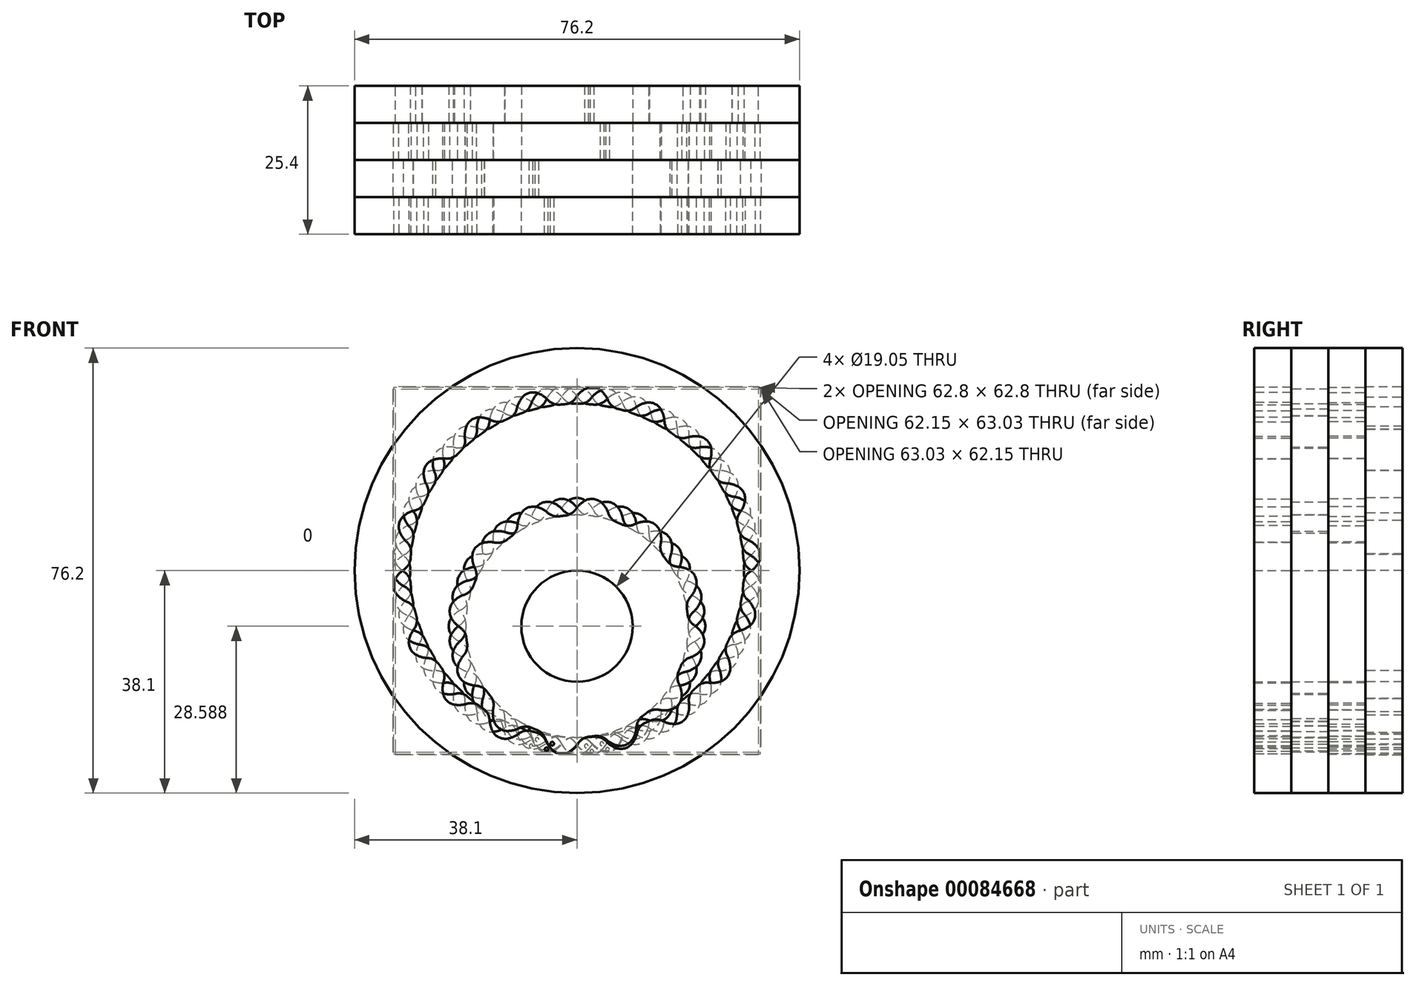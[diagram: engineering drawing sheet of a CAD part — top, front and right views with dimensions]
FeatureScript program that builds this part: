
annotation { "Feature Type Name" : "Feature", "Feature Type Description" : "" }
export const myFeature = defineFeature(function(context is Context, id is Id, definition is map)
    precondition{}
    {
        {
            var Q0;
            Q0=qCreatedBy(makeId("Front.planeOp"),FACE);
            var sketch = newSketch(context, id + "F0", { "sketchPlane" : qUnion([Q0])});
            skCircle(sketch, "E0", {"center": v(0, 0) * mm, "radius": 38.1 * mm});
            skCircle(sketch, "E1", {"center": v(0, 0) * mm, "radius": 28.58 * mm});
            skCircle(sketch, "E2", {"center": v(0, 0) * mm, "radius": 19.05 * mm});
            skCircle(sketch, "E3", {"center": v(0, 0) * mm, "radius": 9.53 * mm});
            skArc(sketch, "E4", {"start": v(0, -22.23) * mm, "mid": v(2.06, -20.95) * mm, "end": v(3.16, -18.79) * mm});
            skArc(sketch, "E5", {"start": v(-3.16, -18.79) * mm, "mid": v(-2.06, -20.95) * mm, "end": v(0, -22.23) * mm});
            skArc(sketch, "E6", {"start": v(0, -31.74) * mm, "mid": v(2.04, -30.5) * mm, "end": v(3.16, -28.4) * mm});
            skArc(sketch, "E7", {"start": v(-3.16, -28.4) * mm, "mid": v(-2.04, -30.5) * mm, "end": v(0, -31.74) * mm});
            skArc(sketch, "E8.1.0", {"start": v(6.65, -17.85) * mm, "mid": v(8.69, -19.17) * mm, "end": v(11.11, -19.25) * mm});
            skArc(sketch, "E8.1.1", {"start": v(11.11, -19.25) * mm, "mid": v(12.26, -17.11) * mm, "end": v(12.13, -14.69) * mm});
            skArc(sketch, "E8.2.0", {"start": v(14.69, -12.13) * mm, "mid": v(17.11, -12.26) * mm, "end": v(19.25, -11.11) * mm});
            skArc(sketch, "E8.2.1", {"start": v(19.25, -11.11) * mm, "mid": v(19.17, -8.69) * mm, "end": v(17.85, -6.65) * mm});
            skArc(sketch, "E8.3.0", {"start": v(18.79, -3.16) * mm, "mid": v(20.95, -2.06) * mm, "end": v(22.23, 0) * mm});
            skArc(sketch, "E8.3.1", {"start": v(22.23, 0) * mm, "mid": v(20.95, 2.06) * mm, "end": v(18.79, 3.16) * mm});
            skArc(sketch, "E8.4.0", {"start": v(17.85, 6.65) * mm, "mid": v(19.17, 8.69) * mm, "end": v(19.25, 11.11) * mm});
            skArc(sketch, "E8.4.1", {"start": v(19.25, 11.11) * mm, "mid": v(17.11, 12.26) * mm, "end": v(14.69, 12.13) * mm});
            skArc(sketch, "E8.5.0", {"start": v(12.13, 14.69) * mm, "mid": v(12.26, 17.11) * mm, "end": v(11.11, 19.25) * mm});
            skArc(sketch, "E8.5.1", {"start": v(11.11, 19.25) * mm, "mid": v(8.69, 19.17) * mm, "end": v(6.65, 17.85) * mm});
            skArc(sketch, "E8.6.0", {"start": v(3.16, 18.79) * mm, "mid": v(2.06, 20.95) * mm, "end": v(0, 22.23) * mm});
            skArc(sketch, "E8.6.1", {"start": v(0, 22.23) * mm, "mid": v(-2.06, 20.95) * mm, "end": v(-3.16, 18.79) * mm});
            skArc(sketch, "E8.7.0", {"start": v(-6.65, 17.85) * mm, "mid": v(-8.69, 19.17) * mm, "end": v(-11.11, 19.25) * mm});
            skArc(sketch, "E8.7.1", {"start": v(-11.11, 19.25) * mm, "mid": v(-12.26, 17.11) * mm, "end": v(-12.13, 14.69) * mm});
            skArc(sketch, "E8.8.0", {"start": v(-14.69, 12.13) * mm, "mid": v(-17.11, 12.26) * mm, "end": v(-19.25, 11.11) * mm});
            skArc(sketch, "E8.8.1", {"start": v(-19.25, 11.11) * mm, "mid": v(-19.17, 8.69) * mm, "end": v(-17.85, 6.65) * mm});
            skArc(sketch, "E8.9.0", {"start": v(-18.79, 3.16) * mm, "mid": v(-20.95, 2.06) * mm, "end": v(-22.23, 0) * mm});
            skArc(sketch, "E8.9.1", {"start": v(-22.23, 0) * mm, "mid": v(-20.95, -2.06) * mm, "end": v(-18.79, -3.16) * mm});
            skArc(sketch, "E8.10.0", {"start": v(-17.85, -6.65) * mm, "mid": v(-19.17, -8.69) * mm, "end": v(-19.25, -11.11) * mm});
            skArc(sketch, "E8.10.1", {"start": v(-19.25, -11.11) * mm, "mid": v(-17.11, -12.26) * mm, "end": v(-14.69, -12.13) * mm});
            skArc(sketch, "E8.11.0", {"start": v(-12.13, -14.69) * mm, "mid": v(-12.26, -17.11) * mm, "end": v(-11.11, -19.25) * mm});
            skArc(sketch, "E8.11.1", {"start": v(-11.11, -19.25) * mm, "mid": v(-8.69, -19.17) * mm, "end": v(-6.65, -17.85) * mm});
            skArc(sketch, "E9.1.0", {"start": v(6.74, -27.77) * mm, "mid": v(8.51, -29.37) * mm, "end": v(10.86, -29.83) * mm});
            skArc(sketch, "E9.1.1", {"start": v(10.86, -29.83) * mm, "mid": v(12.35, -27.97) * mm, "end": v(12.69, -25.6) * mm});
            skArc(sketch, "E9.2.0", {"start": v(15.83, -23.79) * mm, "mid": v(18.05, -24.68) * mm, "end": v(20.4, -24.32) * mm});
            skArc(sketch, "E9.2.1", {"start": v(20.4, -24.32) * mm, "mid": v(21.17, -22.06) * mm, "end": v(20.68, -19.72) * mm});
            skArc(sketch, "E9.3.0", {"start": v(23.01, -16.94) * mm, "mid": v(25.4, -17.02) * mm, "end": v(27.5, -15.87) * mm});
            skArc(sketch, "E9.3.1", {"start": v(27.5, -15.87) * mm, "mid": v(27.44, -13.48) * mm, "end": v(26.18, -11.46) * mm});
            skArc(sketch, "E9.4.0", {"start": v(27.42, -8.05) * mm, "mid": v(29.69, -7.3) * mm, "end": v(31.26, -5.51) * mm});
            skArc(sketch, "E9.4.1", {"start": v(31.26, -5.51) * mm, "mid": v(30.4, -3.29) * mm, "end": v(28.52, -1.82) * mm});
            skArc(sketch, "E9.5.0", {"start": v(28.52, 1.82) * mm, "mid": v(30.4, 3.29) * mm, "end": v(31.26, 5.51) * mm});
            skArc(sketch, "E9.5.1", {"start": v(31.26, 5.51) * mm, "mid": v(29.69, 7.3) * mm, "end": v(27.42, 8.05) * mm});
            skArc(sketch, "E9.6.0", {"start": v(26.18, 11.46) * mm, "mid": v(27.44, 13.48) * mm, "end": v(27.5, 15.87) * mm});
            skArc(sketch, "E9.6.1", {"start": v(27.5, 15.87) * mm, "mid": v(25.4, 17.02) * mm, "end": v(23.01, 16.94) * mm});
            skArc(sketch, "E9.7.0", {"start": v(20.68, 19.72) * mm, "mid": v(21.17, 22.06) * mm, "end": v(20.4, 24.32) * mm});
            skArc(sketch, "E9.7.1", {"start": v(20.4, 24.32) * mm, "mid": v(18.05, 24.68) * mm, "end": v(15.83, 23.79) * mm});
            skArc(sketch, "E9.8.0", {"start": v(12.69, 25.6) * mm, "mid": v(12.35, 27.97) * mm, "end": v(10.86, 29.83) * mm});
            skArc(sketch, "E9.8.1", {"start": v(10.86, 29.83) * mm, "mid": v(8.51, 29.37) * mm, "end": v(6.74, 27.77) * mm});
            skArc(sketch, "E9.9.0", {"start": v(3.16, 28.4) * mm, "mid": v(2.04, 30.5) * mm, "end": v(0, 31.74) * mm});
            skArc(sketch, "E9.9.1", {"start": v(0, 31.74) * mm, "mid": v(-2.04, 30.5) * mm, "end": v(-3.16, 28.4) * mm});
            skArc(sketch, "E9.10.0", {"start": v(-6.74, 27.77) * mm, "mid": v(-8.51, 29.37) * mm, "end": v(-10.86, 29.83) * mm});
            skArc(sketch, "E9.10.1", {"start": v(-10.86, 29.83) * mm, "mid": v(-12.35, 27.97) * mm, "end": v(-12.69, 25.6) * mm});
            skArc(sketch, "E9.11.0", {"start": v(-15.83, 23.79) * mm, "mid": v(-18.05, 24.68) * mm, "end": v(-20.4, 24.32) * mm});
            skArc(sketch, "E9.11.1", {"start": v(-20.4, 24.32) * mm, "mid": v(-21.17, 22.06) * mm, "end": v(-20.68, 19.72) * mm});
            skArc(sketch, "E9.12.0", {"start": v(-23.01, 16.94) * mm, "mid": v(-25.4, 17.02) * mm, "end": v(-27.5, 15.87) * mm});
            skArc(sketch, "E9.12.1", {"start": v(-27.5, 15.87) * mm, "mid": v(-27.44, 13.48) * mm, "end": v(-26.18, 11.46) * mm});
            skArc(sketch, "E9.13.0", {"start": v(-27.42, 8.05) * mm, "mid": v(-29.69, 7.3) * mm, "end": v(-31.26, 5.51) * mm});
            skArc(sketch, "E9.13.1", {"start": v(-31.26, 5.51) * mm, "mid": v(-30.4, 3.29) * mm, "end": v(-28.52, 1.82) * mm});
            skArc(sketch, "E9.14.0", {"start": v(-28.52, -1.82) * mm, "mid": v(-30.4, -3.29) * mm, "end": v(-31.26, -5.51) * mm});
            skArc(sketch, "E9.14.1", {"start": v(-31.26, -5.51) * mm, "mid": v(-29.69, -7.3) * mm, "end": v(-27.42, -8.05) * mm});
            skArc(sketch, "E9.15.0", {"start": v(-26.18, -11.46) * mm, "mid": v(-27.44, -13.48) * mm, "end": v(-27.5, -15.87) * mm});
            skArc(sketch, "E9.15.1", {"start": v(-27.5, -15.87) * mm, "mid": v(-25.4, -17.02) * mm, "end": v(-23.01, -16.94) * mm});
            skArc(sketch, "E9.16.0", {"start": v(-20.68, -19.72) * mm, "mid": v(-21.17, -22.06) * mm, "end": v(-20.4, -24.32) * mm});
            skArc(sketch, "E9.16.1", {"start": v(-20.4, -24.32) * mm, "mid": v(-18.05, -24.68) * mm, "end": v(-15.83, -23.79) * mm});
            skArc(sketch, "E9.17.0", {"start": v(-12.69, -25.6) * mm, "mid": v(-12.35, -27.97) * mm, "end": v(-10.86, -29.83) * mm});
            skArc(sketch, "E9.17.1", {"start": v(-10.86, -29.83) * mm, "mid": v(-8.51, -29.37) * mm, "end": v(-6.74, -27.77) * mm});
            skCircle(sketch, "E10", {"center": v(1.58, -20.5) * mm, "radius": 0.32 * mm});
            skCircle(sketch, "E11", {"center": v(2.53, -30.95) * mm, "radius": 0.32 * mm});
            skSolve(sketch);
        }
        {
            var Q0;
            Q0=makeQuery(id+"F0.imprint","IMPRINT",FACE,{"disambiguationData":[TD([[makeQuery(id+"F0.imprint","IMPRINT",EDGE,{"derivedFrom":sQuery(id+"F0.wireOp",EDGE,"E3")}),-1.0]])]});
            var Q1;
            {var subQ0=sQuery(id+"F0.wireOp",EDGE,"E8.6.0");Q1=makeQuery(id+"F0.imprint","IMPRINT",FACE,{"disambiguationData":[TD([[makeQuery(id+"F0.imprint","IMPRINT",EDGE,{"derivedFrom":subQ0}),1.0]])]});}
            var Q2;
            {var subQ0=sQuery(id+"F0.wireOp",EDGE,"E8.7.0");Q2=makeQuery(id+"F0.imprint","IMPRINT",FACE,{"disambiguationData":[TD([[makeQuery(id+"F0.imprint","IMPRINT",EDGE,{"derivedFrom":subQ0}),1.0]])]});}
            var Q3;
            {var subQ0=sQuery(id+"F0.wireOp",EDGE,"E8.8.0");Q3=makeQuery(id+"F0.imprint","IMPRINT",FACE,{"disambiguationData":[TD([[makeQuery(id+"F0.imprint","IMPRINT",EDGE,{"derivedFrom":subQ0}),1.0]])]});}
            var Q4;
            {var subQ0=sQuery(id+"F0.wireOp",EDGE,"E8.9.0");Q4=makeQuery(id+"F0.imprint","IMPRINT",FACE,{"disambiguationData":[TD([[makeQuery(id+"F0.imprint","IMPRINT",EDGE,{"derivedFrom":subQ0}),1.0]])]});}
            var Q5;
            {var subQ0=sQuery(id+"F0.wireOp",EDGE,"E8.10.0");Q5=makeQuery(id+"F0.imprint","IMPRINT",FACE,{"disambiguationData":[TD([[makeQuery(id+"F0.imprint","IMPRINT",EDGE,{"derivedFrom":subQ0}),1.0]])]});}
            var Q6;
            {var subQ0=sQuery(id+"F0.wireOp",EDGE,"E8.5.0");Q6=makeQuery(id+"F0.imprint","IMPRINT",FACE,{"disambiguationData":[TD([[makeQuery(id+"F0.imprint","IMPRINT",EDGE,{"derivedFrom":subQ0}),1.0]])]});}
            var Q7;
            {var subQ0=sQuery(id+"F0.wireOp",EDGE,"E8.4.0");Q7=makeQuery(id+"F0.imprint","IMPRINT",FACE,{"disambiguationData":[TD([[makeQuery(id+"F0.imprint","IMPRINT",EDGE,{"derivedFrom":subQ0}),1.0]])]});}
            var Q8;
            {var subQ0=sQuery(id+"F0.wireOp",EDGE,"E8.3.0");Q8=makeQuery(id+"F0.imprint","IMPRINT",FACE,{"disambiguationData":[TD([[makeQuery(id+"F0.imprint","IMPRINT",EDGE,{"derivedFrom":subQ0}),1.0]])]});}
            var Q9;
            {var subQ0=sQuery(id+"F0.wireOp",EDGE,"E8.2.0");Q9=makeQuery(id+"F0.imprint","IMPRINT",FACE,{"disambiguationData":[TD([[makeQuery(id+"F0.imprint","IMPRINT",EDGE,{"derivedFrom":subQ0}),1.0]])]});}
            var Q10;
            {var subQ0=sQuery(id+"F0.wireOp",EDGE,"E8.11.0");Q10=makeQuery(id+"F0.imprint","IMPRINT",FACE,{"disambiguationData":[TD([[makeQuery(id+"F0.imprint","IMPRINT",EDGE,{"derivedFrom":subQ0}),1.0]])]});}
            var Q11;
            {var subQ0=sQuery(id+"F0.wireOp",EDGE,"E4");Q11=makeQuery(id+"F0.imprint","IMPRINT",FACE,{"disambiguationData":[TD([[makeQuery(id+"F0.imprint","IMPRINT",EDGE,{"derivedFrom":subQ0}),1.0]])]});}
            var Q12;
            {var subQ0=sQuery(id+"F0.wireOp",EDGE,"E8.1.0");Q12=makeQuery(id+"F0.imprint","IMPRINT",FACE,{"disambiguationData":[TD([[makeQuery(id+"F0.imprint","IMPRINT",EDGE,{"derivedFrom":subQ0}),1.0]])]});}
            extrude(context, id + "F1", {"entities" : qUnion([Q0, Q1, Q2, Q3, Q4, Q5, Q6, Q7, Q8, Q9, Q10, Q11, Q12]), "oppositeDirection" : true, "depth" : 6.35 * mm});
        }
        {
            var Q0;
            Q0=makeQuery(id+"F0.imprint","IMPRINT",FACE,{"disambiguationData":[TD([[makeQuery(id+"F0.imprint","IMPRINT",EDGE,{"derivedFrom":sQuery(id+"F0.wireOp",EDGE,"E0")}),1.0]])]});
            extrude(context, id + "F2", {"entities" : qUnion([Q0]), "oppositeDirection" : true, "depth" : 6.35 * mm});
        }
        {
            var Q0;
            Q0=makeQuery(id+"F1.opExtrude","SWEPT_EDGE",EDGE,{"disambiguationData":[OSD([sQuery(id+"F0.wireOp",EDGE,"E2"),sQuery(id+"F0.wireOp",EDGE,"E5")])]});
            var Q1;
            Q1=makeQuery(id+"F1.opExtrude","SWEPT_EDGE",EDGE,{"disambiguationData":[OSD([sQuery(id+"F0.wireOp",EDGE,"E2"),sQuery(id+"F0.wireOp",EDGE,"E4")])]});
            var Q2;
            Q2=makeQuery(id+"F1.opExtrude","SWEPT_EDGE",EDGE,{"disambiguationData":[OSD([sQuery(id+"F0.wireOp",EDGE,"E2"),sQuery(id+"F0.wireOp",EDGE,"E8.1.0")])]});
            var Q3;
            Q3=makeQuery(id+"F1.opExtrude","SWEPT_EDGE",EDGE,{"disambiguationData":[OSD([sQuery(id+"F0.wireOp",EDGE,"E2"),sQuery(id+"F0.wireOp",EDGE,"E8.11.1")])]});
            var Q4;
            Q4=makeQuery(id+"F1.opExtrude","SWEPT_EDGE",EDGE,{"disambiguationData":[OSD([sQuery(id+"F0.wireOp",EDGE,"E2"),sQuery(id+"F0.wireOp",EDGE,"E8.11.0")])]});
            var Q5;
            Q5=makeQuery(id+"F1.opExtrude","SWEPT_EDGE",EDGE,{"disambiguationData":[OSD([sQuery(id+"F0.wireOp",EDGE,"E2"),sQuery(id+"F0.wireOp",EDGE,"E8.10.1")])]});
            var Q6;
            Q6=makeQuery(id+"F1.opExtrude","SWEPT_EDGE",EDGE,{"disambiguationData":[OSD([sQuery(id+"F0.wireOp",EDGE,"E2"),sQuery(id+"F0.wireOp",EDGE,"E8.1.1")])]});
            var Q7;
            Q7=makeQuery(id+"F1.opExtrude","SWEPT_EDGE",EDGE,{"disambiguationData":[OSD([sQuery(id+"F0.wireOp",EDGE,"E2"),sQuery(id+"F0.wireOp",EDGE,"E8.2.0")])]});
            var Q8;
            Q8=makeQuery(id+"F1.opExtrude","SWEPT_EDGE",EDGE,{"disambiguationData":[OSD([sQuery(id+"F0.wireOp",EDGE,"E2"),sQuery(id+"F0.wireOp",EDGE,"E8.2.1")])]});
            var Q9;
            Q9=makeQuery(id+"F1.opExtrude","SWEPT_EDGE",EDGE,{"disambiguationData":[OSD([sQuery(id+"F0.wireOp",EDGE,"E2"),sQuery(id+"F0.wireOp",EDGE,"E8.10.0")])]});
            var Q10;
            Q10=makeQuery(id+"F1.opExtrude","SWEPT_EDGE",EDGE,{"disambiguationData":[OSD([sQuery(id+"F0.wireOp",EDGE,"E2"),sQuery(id+"F0.wireOp",EDGE,"E8.9.1")])]});
            var Q11;
            Q11=makeQuery(id+"F1.opExtrude","SWEPT_EDGE",EDGE,{"disambiguationData":[OSD([sQuery(id+"F0.wireOp",EDGE,"E2"),sQuery(id+"F0.wireOp",EDGE,"E8.9.0")])]});
            var Q12;
            Q12=makeQuery(id+"F1.opExtrude","SWEPT_EDGE",EDGE,{"disambiguationData":[OSD([sQuery(id+"F0.wireOp",EDGE,"E2"),sQuery(id+"F0.wireOp",EDGE,"E8.8.1")])]});
            var Q13;
            Q13=makeQuery(id+"F1.opExtrude","SWEPT_EDGE",EDGE,{"disambiguationData":[OSD([sQuery(id+"F0.wireOp",EDGE,"E2"),sQuery(id+"F0.wireOp",EDGE,"E8.8.0")])]});
            var Q14;
            Q14=makeQuery(id+"F1.opExtrude","SWEPT_EDGE",EDGE,{"disambiguationData":[OSD([sQuery(id+"F0.wireOp",EDGE,"E2"),sQuery(id+"F0.wireOp",EDGE,"E8.7.1")])]});
            var Q15;
            Q15=makeQuery(id+"F1.opExtrude","SWEPT_EDGE",EDGE,{"disambiguationData":[OSD([sQuery(id+"F0.wireOp",EDGE,"E2"),sQuery(id+"F0.wireOp",EDGE,"E8.7.0")])]});
            var Q16;
            Q16=makeQuery(id+"F1.opExtrude","SWEPT_EDGE",EDGE,{"disambiguationData":[OSD([sQuery(id+"F0.wireOp",EDGE,"E2"),sQuery(id+"F0.wireOp",EDGE,"E8.6.1")])]});
            var Q17;
            Q17=makeQuery(id+"F1.opExtrude","SWEPT_EDGE",EDGE,{"disambiguationData":[OSD([sQuery(id+"F0.wireOp",EDGE,"E2"),sQuery(id+"F0.wireOp",EDGE,"E8.6.0")])]});
            var Q18;
            Q18=makeQuery(id+"F1.opExtrude","SWEPT_EDGE",EDGE,{"disambiguationData":[OSD([sQuery(id+"F0.wireOp",EDGE,"E2"),sQuery(id+"F0.wireOp",EDGE,"E8.5.1")])]});
            var Q19;
            Q19=makeQuery(id+"F1.opExtrude","SWEPT_EDGE",EDGE,{"disambiguationData":[OSD([sQuery(id+"F0.wireOp",EDGE,"E2"),sQuery(id+"F0.wireOp",EDGE,"E8.5.0")])]});
            var Q20;
            Q20=makeQuery(id+"F1.opExtrude","SWEPT_EDGE",EDGE,{"disambiguationData":[OSD([sQuery(id+"F0.wireOp",EDGE,"E2"),sQuery(id+"F0.wireOp",EDGE,"E8.4.1")])]});
            var Q21;
            Q21=makeQuery(id+"F1.opExtrude","SWEPT_EDGE",EDGE,{"disambiguationData":[OSD([sQuery(id+"F0.wireOp",EDGE,"E2"),sQuery(id+"F0.wireOp",EDGE,"E8.4.0")])]});
            var Q22;
            Q22=makeQuery(id+"F1.opExtrude","SWEPT_EDGE",EDGE,{"disambiguationData":[OSD([sQuery(id+"F0.wireOp",EDGE,"E2"),sQuery(id+"F0.wireOp",EDGE,"E8.3.1")])]});
            var Q23;
            Q23=makeQuery(id+"F1.opExtrude","SWEPT_EDGE",EDGE,{"disambiguationData":[OSD([sQuery(id+"F0.wireOp",EDGE,"E2"),sQuery(id+"F0.wireOp",EDGE,"E8.3.0")])]});
            fillet(context, id + "F3", {"entities" : qUnion([Q0, Q1, Q2, Q3, Q4, Q5, Q6, Q7, Q8, Q9, Q10, Q11, Q12, Q13, Q14, Q15, Q16, Q17, Q18, Q19, Q20, Q21, Q22, Q23]), "radius" : 2.54 * mm, "tangentPropagation" : true, "allowEdgeOverflow" : false});
        }
        {
            var Q0;
            Q0=makeQuery(id+"F1.opExtrude","SWEPT_EDGE",EDGE,{"disambiguationData":[OSD([sQuery(id+"F0.wireOp",EDGE,"E4"),sQuery(id+"F0.wireOp",EDGE,"E5")])]});
            var Q1;
            Q1=makeQuery(id+"F1.opExtrude","SWEPT_EDGE",EDGE,{"disambiguationData":[OSD([sQuery(id+"F0.wireOp",EDGE,"E8.1.0"),sQuery(id+"F0.wireOp",EDGE,"E8.1.1")])]});
            var Q2;
            Q2=makeQuery(id+"F1.opExtrude","SWEPT_EDGE",EDGE,{"disambiguationData":[OSD([sQuery(id+"F0.wireOp",EDGE,"E8.11.0"),sQuery(id+"F0.wireOp",EDGE,"E8.11.1")])]});
            var Q3;
            Q3=makeQuery(id+"F1.opExtrude","SWEPT_EDGE",EDGE,{"disambiguationData":[OSD([sQuery(id+"F0.wireOp",EDGE,"E8.10.0"),sQuery(id+"F0.wireOp",EDGE,"E8.10.1")])]});
            var Q4;
            Q4=makeQuery(id+"F1.opExtrude","SWEPT_EDGE",EDGE,{"disambiguationData":[OSD([sQuery(id+"F0.wireOp",EDGE,"E8.2.0"),sQuery(id+"F0.wireOp",EDGE,"E8.2.1")])]});
            var Q5;
            Q5=makeQuery(id+"F1.opExtrude","SWEPT_EDGE",EDGE,{"disambiguationData":[OSD([sQuery(id+"F0.wireOp",EDGE,"E8.3.0"),sQuery(id+"F0.wireOp",EDGE,"E8.3.1")])]});
            var Q6;
            Q6=makeQuery(id+"F1.opExtrude","SWEPT_EDGE",EDGE,{"disambiguationData":[OSD([sQuery(id+"F0.wireOp",EDGE,"E8.9.0"),sQuery(id+"F0.wireOp",EDGE,"E8.9.1")])]});
            var Q7;
            Q7=makeQuery(id+"F1.opExtrude","SWEPT_EDGE",EDGE,{"disambiguationData":[OSD([sQuery(id+"F0.wireOp",EDGE,"E8.8.0"),sQuery(id+"F0.wireOp",EDGE,"E8.8.1")])]});
            var Q8;
            Q8=makeQuery(id+"F1.opExtrude","SWEPT_EDGE",EDGE,{"disambiguationData":[OSD([sQuery(id+"F0.wireOp",EDGE,"E8.7.0"),sQuery(id+"F0.wireOp",EDGE,"E8.7.1")])]});
            var Q9;
            Q9=makeQuery(id+"F1.opExtrude","SWEPT_EDGE",EDGE,{"disambiguationData":[OSD([sQuery(id+"F0.wireOp",EDGE,"E8.6.0"),sQuery(id+"F0.wireOp",EDGE,"E8.6.1")])]});
            var Q10;
            Q10=makeQuery(id+"F1.opExtrude","SWEPT_EDGE",EDGE,{"disambiguationData":[OSD([sQuery(id+"F0.wireOp",EDGE,"E8.5.0"),sQuery(id+"F0.wireOp",EDGE,"E8.5.1")])]});
            var Q11;
            Q11=makeQuery(id+"F1.opExtrude","SWEPT_EDGE",EDGE,{"disambiguationData":[OSD([sQuery(id+"F0.wireOp",EDGE,"E8.4.0"),sQuery(id+"F0.wireOp",EDGE,"E8.4.1")])]});
            fillet(context, id + "F4", {"entities" : qUnion([Q0, Q1, Q2, Q3, Q4, Q5, Q6, Q7, Q8, Q9, Q10, Q11]), "radius" : 2.5 * mm, "tangentPropagation" : true, "allowEdgeOverflow" : false});
        }
        {
            var Q0;
            Q0=makeQuery(id+"F2.opExtrude","SWEPT_EDGE",EDGE,{"disambiguationData":[OSD([sQuery(id+"F0.wireOp",EDGE,"E1"),sQuery(id+"F0.wireOp",EDGE,"E6")])]});
            var Q1;
            Q1=makeQuery(id+"F2.opExtrude","SWEPT_EDGE",EDGE,{"disambiguationData":[OSD([sQuery(id+"F0.wireOp",EDGE,"E1"),sQuery(id+"F0.wireOp",EDGE,"E9.1.1")])]});
            var Q2;
            Q2=makeQuery(id+"F2.opExtrude","SWEPT_EDGE",EDGE,{"disambiguationData":[OSD([sQuery(id+"F0.wireOp",EDGE,"E1"),sQuery(id+"F0.wireOp",EDGE,"E9.2.1")])]});
            var Q3;
            Q3=makeQuery(id+"F2.opExtrude","SWEPT_EDGE",EDGE,{"disambiguationData":[OSD([sQuery(id+"F0.wireOp",EDGE,"E1"),sQuery(id+"F0.wireOp",EDGE,"E9.17.1")])]});
            var Q4;
            Q4=makeQuery(id+"F2.opExtrude","SWEPT_EDGE",EDGE,{"disambiguationData":[OSD([sQuery(id+"F0.wireOp",EDGE,"E1"),sQuery(id+"F0.wireOp",EDGE,"E9.16.1")])]});
            var Q5;
            Q5=makeQuery(id+"F2.opExtrude","SWEPT_EDGE",EDGE,{"disambiguationData":[OSD([sQuery(id+"F0.wireOp",EDGE,"E1"),sQuery(id+"F0.wireOp",EDGE,"E9.15.1")])]});
            var Q6;
            Q6=makeQuery(id+"F2.opExtrude","SWEPT_EDGE",EDGE,{"disambiguationData":[OSD([sQuery(id+"F0.wireOp",EDGE,"E1"),sQuery(id+"F0.wireOp",EDGE,"E9.14.1")])]});
            var Q7;
            Q7=makeQuery(id+"F2.opExtrude","SWEPT_EDGE",EDGE,{"disambiguationData":[OSD([sQuery(id+"F0.wireOp",EDGE,"E1"),sQuery(id+"F0.wireOp",EDGE,"E9.3.1")])]});
            var Q8;
            Q8=makeQuery(id+"F2.opExtrude","SWEPT_EDGE",EDGE,{"disambiguationData":[OSD([sQuery(id+"F0.wireOp",EDGE,"E1"),sQuery(id+"F0.wireOp",EDGE,"E9.4.1")])]});
            var Q9;
            Q9=makeQuery(id+"F2.opExtrude","SWEPT_EDGE",EDGE,{"disambiguationData":[OSD([sQuery(id+"F0.wireOp",EDGE,"E1"),sQuery(id+"F0.wireOp",EDGE,"E9.5.1")])]});
            var Q10;
            Q10=makeQuery(id+"F2.opExtrude","SWEPT_EDGE",EDGE,{"disambiguationData":[OSD([sQuery(id+"F0.wireOp",EDGE,"E1"),sQuery(id+"F0.wireOp",EDGE,"E9.6.1")])]});
            var Q11;
            Q11=makeQuery(id+"F2.opExtrude","SWEPT_EDGE",EDGE,{"disambiguationData":[OSD([sQuery(id+"F0.wireOp",EDGE,"E1"),sQuery(id+"F0.wireOp",EDGE,"E9.13.1")])]});
            var Q12;
            Q12=makeQuery(id+"F2.opExtrude","SWEPT_EDGE",EDGE,{"disambiguationData":[OSD([sQuery(id+"F0.wireOp",EDGE,"E1"),sQuery(id+"F0.wireOp",EDGE,"E9.12.1")])]});
            var Q13;
            Q13=makeQuery(id+"F2.opExtrude","SWEPT_EDGE",EDGE,{"disambiguationData":[OSD([sQuery(id+"F0.wireOp",EDGE,"E1"),sQuery(id+"F0.wireOp",EDGE,"E9.11.1")])]});
            var Q14;
            Q14=makeQuery(id+"F2.opExtrude","SWEPT_EDGE",EDGE,{"disambiguationData":[OSD([sQuery(id+"F0.wireOp",EDGE,"E1"),sQuery(id+"F0.wireOp",EDGE,"E9.10.1")])]});
            var Q15;
            Q15=makeQuery(id+"F2.opExtrude","SWEPT_EDGE",EDGE,{"disambiguationData":[OSD([sQuery(id+"F0.wireOp",EDGE,"E1"),sQuery(id+"F0.wireOp",EDGE,"E9.9.1")])]});
            var Q16;
            Q16=makeQuery(id+"F2.opExtrude","SWEPT_EDGE",EDGE,{"disambiguationData":[OSD([sQuery(id+"F0.wireOp",EDGE,"E1"),sQuery(id+"F0.wireOp",EDGE,"E9.8.1")])]});
            var Q17;
            Q17=makeQuery(id+"F2.opExtrude","SWEPT_EDGE",EDGE,{"disambiguationData":[OSD([sQuery(id+"F0.wireOp",EDGE,"E1"),sQuery(id+"F0.wireOp",EDGE,"E9.7.1")])]});
            fillet(context, id + "F5", {"entities" : qUnion([Q0, Q1, Q2, Q3, Q4, Q5, Q6, Q7, Q8, Q9, Q10, Q11, Q12, Q13, Q14, Q15, Q16, Q17]), "radius" : 2.54 * mm, "tangentPropagation" : true, "allowEdgeOverflow" : false});
        }
        {
            var Q0;
            Q0=makeQuery(id+"F2.opExtrude","SWEPT_EDGE",EDGE,{"disambiguationData":[OSD([sQuery(id+"F0.wireOp",EDGE,"E1"),sQuery(id+"F0.wireOp",EDGE,"E7")])]});
            var Q1;
            Q1=makeQuery(id+"F2.opExtrude","SWEPT_EDGE",EDGE,{"disambiguationData":[OSD([sQuery(id+"F0.wireOp",EDGE,"E1"),sQuery(id+"F0.wireOp",EDGE,"E9.1.0")])]});
            var Q2;
            Q2=makeQuery(id+"F2.opExtrude","SWEPT_EDGE",EDGE,{"disambiguationData":[OSD([sQuery(id+"F0.wireOp",EDGE,"E1"),sQuery(id+"F0.wireOp",EDGE,"E9.17.0")])]});
            var Q3;
            Q3=makeQuery(id+"F2.opExtrude","SWEPT_EDGE",EDGE,{"disambiguationData":[OSD([sQuery(id+"F0.wireOp",EDGE,"E1"),sQuery(id+"F0.wireOp",EDGE,"E9.16.0")])]});
            var Q4;
            Q4=makeQuery(id+"F2.opExtrude","SWEPT_EDGE",EDGE,{"disambiguationData":[OSD([sQuery(id+"F0.wireOp",EDGE,"E1"),sQuery(id+"F0.wireOp",EDGE,"E9.2.0")])]});
            var Q5;
            Q5=makeQuery(id+"F2.opExtrude","SWEPT_EDGE",EDGE,{"disambiguationData":[OSD([sQuery(id+"F0.wireOp",EDGE,"E1"),sQuery(id+"F0.wireOp",EDGE,"E9.3.0")])]});
            var Q6;
            Q6=makeQuery(id+"F2.opExtrude","SWEPT_EDGE",EDGE,{"disambiguationData":[OSD([sQuery(id+"F0.wireOp",EDGE,"E1"),sQuery(id+"F0.wireOp",EDGE,"E9.15.0")])]});
            var Q7;
            Q7=makeQuery(id+"F2.opExtrude","SWEPT_EDGE",EDGE,{"disambiguationData":[OSD([sQuery(id+"F0.wireOp",EDGE,"E1"),sQuery(id+"F0.wireOp",EDGE,"E9.14.0")])]});
            var Q8;
            Q8=makeQuery(id+"F2.opExtrude","SWEPT_EDGE",EDGE,{"disambiguationData":[OSD([sQuery(id+"F0.wireOp",EDGE,"E1"),sQuery(id+"F0.wireOp",EDGE,"E9.4.0")])]});
            var Q9;
            Q9=makeQuery(id+"F2.opExtrude","SWEPT_EDGE",EDGE,{"disambiguationData":[OSD([sQuery(id+"F0.wireOp",EDGE,"E1"),sQuery(id+"F0.wireOp",EDGE,"E9.5.0")])]});
            var Q10;
            Q10=makeQuery(id+"F2.opExtrude","SWEPT_EDGE",EDGE,{"disambiguationData":[OSD([sQuery(id+"F0.wireOp",EDGE,"E1"),sQuery(id+"F0.wireOp",EDGE,"E9.6.0")])]});
            var Q11;
            Q11=makeQuery(id+"F2.opExtrude","SWEPT_EDGE",EDGE,{"disambiguationData":[OSD([sQuery(id+"F0.wireOp",EDGE,"E1"),sQuery(id+"F0.wireOp",EDGE,"E9.7.0")])]});
            var Q12;
            Q12=makeQuery(id+"F2.opExtrude","SWEPT_EDGE",EDGE,{"disambiguationData":[OSD([sQuery(id+"F0.wireOp",EDGE,"E1"),sQuery(id+"F0.wireOp",EDGE,"E9.8.0")])]});
            var Q13;
            Q13=makeQuery(id+"F2.opExtrude","SWEPT_EDGE",EDGE,{"disambiguationData":[OSD([sQuery(id+"F0.wireOp",EDGE,"E1"),sQuery(id+"F0.wireOp",EDGE,"E9.9.0")])]});
            var Q14;
            Q14=makeQuery(id+"F2.opExtrude","SWEPT_EDGE",EDGE,{"disambiguationData":[OSD([sQuery(id+"F0.wireOp",EDGE,"E1"),sQuery(id+"F0.wireOp",EDGE,"E9.10.0")])]});
            var Q15;
            Q15=makeQuery(id+"F2.opExtrude","SWEPT_EDGE",EDGE,{"disambiguationData":[OSD([sQuery(id+"F0.wireOp",EDGE,"E1"),sQuery(id+"F0.wireOp",EDGE,"E9.11.0")])]});
            var Q16;
            Q16=makeQuery(id+"F2.opExtrude","SWEPT_EDGE",EDGE,{"disambiguationData":[OSD([sQuery(id+"F0.wireOp",EDGE,"E1"),sQuery(id+"F0.wireOp",EDGE,"E9.12.0")])]});
            var Q17;
            Q17=makeQuery(id+"F2.opExtrude","SWEPT_EDGE",EDGE,{"disambiguationData":[OSD([sQuery(id+"F0.wireOp",EDGE,"E1"),sQuery(id+"F0.wireOp",EDGE,"E9.13.0")])]});
            fillet(context, id + "F6", {"entities" : qUnion([Q0, Q1, Q2, Q3, Q4, Q5, Q6, Q7, Q8, Q9, Q10, Q11, Q12, Q13, Q14, Q15, Q16, Q17]), "radius" : 2.3 * mm, "tangentPropagation" : true, "allowEdgeOverflow" : false});
        }
        {
            var Q0;
            Q0=makeQuery(id+"F2.opExtrude","SWEPT_EDGE",EDGE,{"disambiguationData":[OSD([sQuery(id+"F0.wireOp",EDGE,"E6"),sQuery(id+"F0.wireOp",EDGE,"E7")])]});
            var Q1;
            Q1=makeQuery(id+"F2.opExtrude","SWEPT_EDGE",EDGE,{"disambiguationData":[OSD([sQuery(id+"F0.wireOp",EDGE,"E9.1.0"),sQuery(id+"F0.wireOp",EDGE,"E9.1.1")])]});
            var Q2;
            Q2=makeQuery(id+"F2.opExtrude","SWEPT_EDGE",EDGE,{"disambiguationData":[OSD([sQuery(id+"F0.wireOp",EDGE,"E9.2.0"),sQuery(id+"F0.wireOp",EDGE,"E9.2.1")])]});
            var Q3;
            Q3=makeQuery(id+"F2.opExtrude","SWEPT_EDGE",EDGE,{"disambiguationData":[OSD([sQuery(id+"F0.wireOp",EDGE,"E9.3.0"),sQuery(id+"F0.wireOp",EDGE,"E9.3.1")])]});
            var Q4;
            Q4=makeQuery(id+"F2.opExtrude","SWEPT_EDGE",EDGE,{"disambiguationData":[OSD([sQuery(id+"F0.wireOp",EDGE,"E9.17.0"),sQuery(id+"F0.wireOp",EDGE,"E9.17.1")])]});
            var Q5;
            Q5=makeQuery(id+"F2.opExtrude","SWEPT_EDGE",EDGE,{"disambiguationData":[OSD([sQuery(id+"F0.wireOp",EDGE,"E9.16.0"),sQuery(id+"F0.wireOp",EDGE,"E9.16.1")])]});
            var Q6;
            Q6=makeQuery(id+"F2.opExtrude","SWEPT_EDGE",EDGE,{"disambiguationData":[OSD([sQuery(id+"F0.wireOp",EDGE,"E9.15.0"),sQuery(id+"F0.wireOp",EDGE,"E9.15.1")])]});
            var Q7;
            Q7=makeQuery(id+"F2.opExtrude","SWEPT_EDGE",EDGE,{"disambiguationData":[OSD([sQuery(id+"F0.wireOp",EDGE,"E9.14.0"),sQuery(id+"F0.wireOp",EDGE,"E9.14.1")])]});
            var Q8;
            Q8=makeQuery(id+"F2.opExtrude","SWEPT_EDGE",EDGE,{"disambiguationData":[OSD([sQuery(id+"F0.wireOp",EDGE,"E9.13.0"),sQuery(id+"F0.wireOp",EDGE,"E9.13.1")])]});
            var Q9;
            Q9=makeQuery(id+"F2.opExtrude","SWEPT_EDGE",EDGE,{"disambiguationData":[OSD([sQuery(id+"F0.wireOp",EDGE,"E9.4.0"),sQuery(id+"F0.wireOp",EDGE,"E9.4.1")])]});
            var Q10;
            Q10=makeQuery(id+"F2.opExtrude","SWEPT_EDGE",EDGE,{"disambiguationData":[OSD([sQuery(id+"F0.wireOp",EDGE,"E9.5.0"),sQuery(id+"F0.wireOp",EDGE,"E9.5.1")])]});
            var Q11;
            Q11=makeQuery(id+"F2.opExtrude","SWEPT_EDGE",EDGE,{"disambiguationData":[OSD([sQuery(id+"F0.wireOp",EDGE,"E9.6.0"),sQuery(id+"F0.wireOp",EDGE,"E9.6.1")])]});
            var Q12;
            Q12=makeQuery(id+"F2.opExtrude","SWEPT_EDGE",EDGE,{"disambiguationData":[OSD([sQuery(id+"F0.wireOp",EDGE,"E9.12.0"),sQuery(id+"F0.wireOp",EDGE,"E9.12.1")])]});
            var Q13;
            Q13=makeQuery(id+"F2.opExtrude","SWEPT_EDGE",EDGE,{"disambiguationData":[OSD([sQuery(id+"F0.wireOp",EDGE,"E9.11.0"),sQuery(id+"F0.wireOp",EDGE,"E9.11.1")])]});
            var Q14;
            Q14=makeQuery(id+"F2.opExtrude","SWEPT_EDGE",EDGE,{"disambiguationData":[OSD([sQuery(id+"F0.wireOp",EDGE,"E9.10.0"),sQuery(id+"F0.wireOp",EDGE,"E9.10.1")])]});
            var Q15;
            Q15=makeQuery(id+"F2.opExtrude","SWEPT_EDGE",EDGE,{"disambiguationData":[OSD([sQuery(id+"F0.wireOp",EDGE,"E9.9.0"),sQuery(id+"F0.wireOp",EDGE,"E9.9.1")])]});
            var Q16;
            Q16=makeQuery(id+"F2.opExtrude","SWEPT_EDGE",EDGE,{"disambiguationData":[OSD([sQuery(id+"F0.wireOp",EDGE,"E9.7.0"),sQuery(id+"F0.wireOp",EDGE,"E9.7.1")])]});
            var Q17;
            Q17=makeQuery(id+"F2.opExtrude","SWEPT_EDGE",EDGE,{"disambiguationData":[OSD([sQuery(id+"F0.wireOp",EDGE,"E9.8.0"),sQuery(id+"F0.wireOp",EDGE,"E9.8.1")])]});
            fillet(context, id + "F7", {"entities" : qUnion([Q0, Q1, Q2, Q3, Q4, Q5, Q6, Q7, Q8, Q9, Q10, Q11, Q12, Q13, Q14, Q15, Q16, Q17]), "radius" : 2.41 * mm, "tangentPropagation" : true, "allowEdgeOverflow" : false});
        }
        {
            var Q0;
            Q0=makeQuery(id+"F1.opExtrude","SWEPT_BODY",BODY,{"disambiguationData":[OSD([sQuery(id+"F0.wireOp",EDGE,"E2"),sQuery(id+"F0.wireOp",EDGE,"E3"),sQuery(id+"F0.wireOp",EDGE,"E4"),sQuery(id+"F0.wireOp",EDGE,"E5"),sQuery(id+"F0.wireOp",EDGE,"E8.1.0"),sQuery(id+"F0.wireOp",EDGE,"E8.1.1"),sQuery(id+"F0.wireOp",EDGE,"E8.2.0"),sQuery(id+"F0.wireOp",EDGE,"E8.2.1"),sQuery(id+"F0.wireOp",EDGE,"E8.3.0"),sQuery(id+"F0.wireOp",EDGE,"E8.3.1"),sQuery(id+"F0.wireOp",EDGE,"E8.4.0"),sQuery(id+"F0.wireOp",EDGE,"E8.4.1"),sQuery(id+"F0.wireOp",EDGE,"E8.5.0"),sQuery(id+"F0.wireOp",EDGE,"E8.5.1"),sQuery(id+"F0.wireOp",EDGE,"E8.6.0"),sQuery(id+"F0.wireOp",EDGE,"E8.6.1"),sQuery(id+"F0.wireOp",EDGE,"E8.7.0"),sQuery(id+"F0.wireOp",EDGE,"E8.7.1"),sQuery(id+"F0.wireOp",EDGE,"E8.8.0"),sQuery(id+"F0.wireOp",EDGE,"E8.8.1"),sQuery(id+"F0.wireOp",EDGE,"E8.9.0"),sQuery(id+"F0.wireOp",EDGE,"E8.9.1"),sQuery(id+"F0.wireOp",EDGE,"E8.10.0"),sQuery(id+"F0.wireOp",EDGE,"E8.10.1"),sQuery(id+"F0.wireOp",EDGE,"E8.11.0"),sQuery(id+"F0.wireOp",EDGE,"E8.11.1"),sQuery(id+"F0.wireOp",EDGE,"E10")])]});
            transform(context, id + "F8", {"entities" : qUnion([Q0]), "transformType" : TransformType.TRANSLATION_3D, "dx" : 0 * mm, "dy" : 0 * mm, "dz" : -9.5 * mm, "makeCopy" : false});
        }
        {
            var Q0;
            Q0=makeQuery(id+"F1.opExtrude","SWEPT_BODY",BODY,{"disambiguationData":[OSD([sQuery(id+"F0.wireOp",EDGE,"E2"),sQuery(id+"F0.wireOp",EDGE,"E3"),sQuery(id+"F0.wireOp",EDGE,"E4"),sQuery(id+"F0.wireOp",EDGE,"E5"),sQuery(id+"F0.wireOp",EDGE,"E8.1.0"),sQuery(id+"F0.wireOp",EDGE,"E8.1.1"),sQuery(id+"F0.wireOp",EDGE,"E8.2.0"),sQuery(id+"F0.wireOp",EDGE,"E8.2.1"),sQuery(id+"F0.wireOp",EDGE,"E8.3.0"),sQuery(id+"F0.wireOp",EDGE,"E8.3.1"),sQuery(id+"F0.wireOp",EDGE,"E8.4.0"),sQuery(id+"F0.wireOp",EDGE,"E8.4.1"),sQuery(id+"F0.wireOp",EDGE,"E8.5.0"),sQuery(id+"F0.wireOp",EDGE,"E8.5.1"),sQuery(id+"F0.wireOp",EDGE,"E8.6.0"),sQuery(id+"F0.wireOp",EDGE,"E8.6.1"),sQuery(id+"F0.wireOp",EDGE,"E8.7.0"),sQuery(id+"F0.wireOp",EDGE,"E8.7.1"),sQuery(id+"F0.wireOp",EDGE,"E8.8.0"),sQuery(id+"F0.wireOp",EDGE,"E8.8.1"),sQuery(id+"F0.wireOp",EDGE,"E8.9.0"),sQuery(id+"F0.wireOp",EDGE,"E8.9.1"),sQuery(id+"F0.wireOp",EDGE,"E8.10.0"),sQuery(id+"F0.wireOp",EDGE,"E8.10.1"),sQuery(id+"F0.wireOp",EDGE,"E8.11.0"),sQuery(id+"F0.wireOp",EDGE,"E8.11.1"),sQuery(id+"F0.wireOp",EDGE,"E10")])]});
            var Q1;
            Q1=makeQuery(id+"F1.opExtrude","CAP_EDGE",EDGE,{"disambiguationData":[OSD([sQuery(id+"F0.wireOp",EDGE,"E3")])],"isStart":true});
            transform(context, id + "F9", {"entities" : qUnion([Q0]), "transformType" : TransformType.ROTATION, "transformAxis" : qUnion([Q1]), "angle" : 0.02 * degree, "makeCopy" : false});
        }
        {
            var Q0;
            Q0=makeQuery(id+"F1.opExtrude","SWEPT_BODY",BODY,{"disambiguationData":[OSD([sQuery(id+"F0.wireOp",EDGE,"E2"),sQuery(id+"F0.wireOp",EDGE,"E3"),sQuery(id+"F0.wireOp",EDGE,"E4"),sQuery(id+"F0.wireOp",EDGE,"E5"),sQuery(id+"F0.wireOp",EDGE,"E8.1.0"),sQuery(id+"F0.wireOp",EDGE,"E8.1.1"),sQuery(id+"F0.wireOp",EDGE,"E8.2.0"),sQuery(id+"F0.wireOp",EDGE,"E8.2.1"),sQuery(id+"F0.wireOp",EDGE,"E8.3.0"),sQuery(id+"F0.wireOp",EDGE,"E8.3.1"),sQuery(id+"F0.wireOp",EDGE,"E8.4.0"),sQuery(id+"F0.wireOp",EDGE,"E8.4.1"),sQuery(id+"F0.wireOp",EDGE,"E8.5.0"),sQuery(id+"F0.wireOp",EDGE,"E8.5.1"),sQuery(id+"F0.wireOp",EDGE,"E8.6.0"),sQuery(id+"F0.wireOp",EDGE,"E8.6.1"),sQuery(id+"F0.wireOp",EDGE,"E8.7.0"),sQuery(id+"F0.wireOp",EDGE,"E8.7.1"),sQuery(id+"F0.wireOp",EDGE,"E8.8.0"),sQuery(id+"F0.wireOp",EDGE,"E8.8.1"),sQuery(id+"F0.wireOp",EDGE,"E8.9.0"),sQuery(id+"F0.wireOp",EDGE,"E8.9.1"),sQuery(id+"F0.wireOp",EDGE,"E8.10.0"),sQuery(id+"F0.wireOp",EDGE,"E8.10.1"),sQuery(id+"F0.wireOp",EDGE,"E8.11.0"),sQuery(id+"F0.wireOp",EDGE,"E8.11.1"),sQuery(id+"F0.wireOp",EDGE,"E10")])]});
            var Q1;
            Q1=makeQuery(id+"F2.opExtrude","SWEPT_BODY",BODY,{"disambiguationData":[OSD([sQuery(id+"F0.wireOp",EDGE,"E0"),sQuery(id+"F0.wireOp",EDGE,"E1"),sQuery(id+"F0.wireOp",EDGE,"E6"),sQuery(id+"F0.wireOp",EDGE,"E7"),sQuery(id+"F0.wireOp",EDGE,"E9.1.0"),sQuery(id+"F0.wireOp",EDGE,"E9.1.1"),sQuery(id+"F0.wireOp",EDGE,"E9.2.0"),sQuery(id+"F0.wireOp",EDGE,"E9.2.1"),sQuery(id+"F0.wireOp",EDGE,"E9.3.0"),sQuery(id+"F0.wireOp",EDGE,"E9.3.1"),sQuery(id+"F0.wireOp",EDGE,"E9.4.0"),sQuery(id+"F0.wireOp",EDGE,"E9.4.1"),sQuery(id+"F0.wireOp",EDGE,"E9.5.0"),sQuery(id+"F0.wireOp",EDGE,"E9.5.1"),sQuery(id+"F0.wireOp",EDGE,"E9.6.0"),sQuery(id+"F0.wireOp",EDGE,"E9.6.1"),sQuery(id+"F0.wireOp",EDGE,"E9.7.0"),sQuery(id+"F0.wireOp",EDGE,"E9.7.1"),sQuery(id+"F0.wireOp",EDGE,"E9.8.0"),sQuery(id+"F0.wireOp",EDGE,"E9.8.1"),sQuery(id+"F0.wireOp",EDGE,"E9.9.0"),sQuery(id+"F0.wireOp",EDGE,"E9.9.1"),sQuery(id+"F0.wireOp",EDGE,"E9.10.0"),sQuery(id+"F0.wireOp",EDGE,"E9.10.1"),sQuery(id+"F0.wireOp",EDGE,"E9.11.0"),sQuery(id+"F0.wireOp",EDGE,"E9.11.1"),sQuery(id+"F0.wireOp",EDGE,"E9.12.0"),sQuery(id+"F0.wireOp",EDGE,"E9.12.1"),sQuery(id+"F0.wireOp",EDGE,"E9.13.0"),sQuery(id+"F0.wireOp",EDGE,"E9.13.1"),sQuery(id+"F0.wireOp",EDGE,"E9.14.0"),sQuery(id+"F0.wireOp",EDGE,"E9.14.1"),sQuery(id+"F0.wireOp",EDGE,"E9.15.0"),sQuery(id+"F0.wireOp",EDGE,"E9.15.1"),sQuery(id+"F0.wireOp",EDGE,"E9.16.0"),sQuery(id+"F0.wireOp",EDGE,"E9.16.1"),sQuery(id+"F0.wireOp",EDGE,"E9.17.0"),sQuery(id+"F0.wireOp",EDGE,"E9.17.1"),sQuery(id+"F0.wireOp",EDGE,"E11")])]});
            transform(context, id + "F10", {"entities" : qUnion([Q0, Q1]), "transformType" : TransformType.TRANSLATION_3D, "dx" : 0 * mm, "dy" : 6.35 * mm, "dz" : 0 * mm, "makeCopy" : true});
        }
        {
            var Q0;
            Q0=makeQuery(id+"F1.opExtrude","SWEPT_BODY",BODY,{"disambiguationData":[OSD([sQuery(id+"F0.wireOp",EDGE,"E2"),sQuery(id+"F0.wireOp",EDGE,"E3"),sQuery(id+"F0.wireOp",EDGE,"E4"),sQuery(id+"F0.wireOp",EDGE,"E5"),sQuery(id+"F0.wireOp",EDGE,"E8.1.0"),sQuery(id+"F0.wireOp",EDGE,"E8.1.1"),sQuery(id+"F0.wireOp",EDGE,"E8.2.0"),sQuery(id+"F0.wireOp",EDGE,"E8.2.1"),sQuery(id+"F0.wireOp",EDGE,"E8.3.0"),sQuery(id+"F0.wireOp",EDGE,"E8.3.1"),sQuery(id+"F0.wireOp",EDGE,"E8.4.0"),sQuery(id+"F0.wireOp",EDGE,"E8.4.1"),sQuery(id+"F0.wireOp",EDGE,"E8.5.0"),sQuery(id+"F0.wireOp",EDGE,"E8.5.1"),sQuery(id+"F0.wireOp",EDGE,"E8.6.0"),sQuery(id+"F0.wireOp",EDGE,"E8.6.1"),sQuery(id+"F0.wireOp",EDGE,"E8.7.0"),sQuery(id+"F0.wireOp",EDGE,"E8.7.1"),sQuery(id+"F0.wireOp",EDGE,"E8.8.0"),sQuery(id+"F0.wireOp",EDGE,"E8.8.1"),sQuery(id+"F0.wireOp",EDGE,"E8.9.0"),sQuery(id+"F0.wireOp",EDGE,"E8.9.1"),sQuery(id+"F0.wireOp",EDGE,"E8.10.0"),sQuery(id+"F0.wireOp",EDGE,"E8.10.1"),sQuery(id+"F0.wireOp",EDGE,"E8.11.0"),sQuery(id+"F0.wireOp",EDGE,"E8.11.1"),sQuery(id+"F0.wireOp",EDGE,"E10")])]});
            var Q1;
            Q1=makeQuery(id+"F1.opExtrude","CAP_EDGE",EDGE,{"disambiguationData":[OSD([sQuery(id+"F0.wireOp",EDGE,"E3")])],"isStart":true});
            transform(context, id + "F11", {"entities" : qUnion([Q0]), "transformType" : TransformType.ROTATION, "transformAxis" : qUnion([Q1]), "angle" : 7.5 * degree, "makeCopy" : false});
        }
        {
            var Q0;
            Q0=makeQuery(id+"F2.opExtrude","SWEPT_BODY",BODY,{"disambiguationData":[OSD([sQuery(id+"F0.wireOp",EDGE,"E0"),sQuery(id+"F0.wireOp",EDGE,"E1"),sQuery(id+"F0.wireOp",EDGE,"E6"),sQuery(id+"F0.wireOp",EDGE,"E7"),sQuery(id+"F0.wireOp",EDGE,"E9.1.0"),sQuery(id+"F0.wireOp",EDGE,"E9.1.1"),sQuery(id+"F0.wireOp",EDGE,"E9.2.0"),sQuery(id+"F0.wireOp",EDGE,"E9.2.1"),sQuery(id+"F0.wireOp",EDGE,"E9.3.0"),sQuery(id+"F0.wireOp",EDGE,"E9.3.1"),sQuery(id+"F0.wireOp",EDGE,"E9.4.0"),sQuery(id+"F0.wireOp",EDGE,"E9.4.1"),sQuery(id+"F0.wireOp",EDGE,"E9.5.0"),sQuery(id+"F0.wireOp",EDGE,"E9.5.1"),sQuery(id+"F0.wireOp",EDGE,"E9.6.0"),sQuery(id+"F0.wireOp",EDGE,"E9.6.1"),sQuery(id+"F0.wireOp",EDGE,"E9.7.0"),sQuery(id+"F0.wireOp",EDGE,"E9.7.1"),sQuery(id+"F0.wireOp",EDGE,"E9.8.0"),sQuery(id+"F0.wireOp",EDGE,"E9.8.1"),sQuery(id+"F0.wireOp",EDGE,"E9.9.0"),sQuery(id+"F0.wireOp",EDGE,"E9.9.1"),sQuery(id+"F0.wireOp",EDGE,"E9.10.0"),sQuery(id+"F0.wireOp",EDGE,"E9.10.1"),sQuery(id+"F0.wireOp",EDGE,"E9.11.0"),sQuery(id+"F0.wireOp",EDGE,"E9.11.1"),sQuery(id+"F0.wireOp",EDGE,"E9.12.0"),sQuery(id+"F0.wireOp",EDGE,"E9.12.1"),sQuery(id+"F0.wireOp",EDGE,"E9.13.0"),sQuery(id+"F0.wireOp",EDGE,"E9.13.1"),sQuery(id+"F0.wireOp",EDGE,"E9.14.0"),sQuery(id+"F0.wireOp",EDGE,"E9.14.1"),sQuery(id+"F0.wireOp",EDGE,"E9.15.0"),sQuery(id+"F0.wireOp",EDGE,"E9.15.1"),sQuery(id+"F0.wireOp",EDGE,"E9.16.0"),sQuery(id+"F0.wireOp",EDGE,"E9.16.1"),sQuery(id+"F0.wireOp",EDGE,"E9.17.0"),sQuery(id+"F0.wireOp",EDGE,"E9.17.1"),sQuery(id+"F0.wireOp",EDGE,"E11")])]});
            var Q1;
            Q1=makeQuery(id+"F2.opExtrude","CAP_EDGE",EDGE,{"disambiguationData":[OSD([sQuery(id+"F0.wireOp",EDGE,"E0")])],"isStart":true});
            transform(context, id + "F12", {"entities" : qUnion([Q0]), "transformType" : TransformType.ROTATION, "transformAxis" : qUnion([Q1]), "angle" : 5 * degree, "makeCopy" : false});
        }
        {
            var Q0;
            Q0=qCreatedBy(makeId("Top.planeOp"),FACE);
            var sketch = newSketch(context, id + "F13", { "sketchPlane" : qUnion([Q0])});
            skCircle(sketch, "E12", {"center": v(0, 0) * mm, "radius": 0.83 * mm});
            skSolve(sketch);
        }
        {
            var Q0;
            Q0=makeQuery(id+"F10.opPattern","COPY",BODY,{"derivedFrom":makeQuery(id+"F1.opExtrude","SWEPT_BODY",BODY,{"disambiguationData":[OSD([sQuery(id+"F0.wireOp",EDGE,"E2"),sQuery(id+"F0.wireOp",EDGE,"E3"),sQuery(id+"F0.wireOp",EDGE,"E4"),sQuery(id+"F0.wireOp",EDGE,"E5"),sQuery(id+"F0.wireOp",EDGE,"E8.1.0"),sQuery(id+"F0.wireOp",EDGE,"E8.1.1"),sQuery(id+"F0.wireOp",EDGE,"E8.2.0"),sQuery(id+"F0.wireOp",EDGE,"E8.2.1"),sQuery(id+"F0.wireOp",EDGE,"E8.3.0"),sQuery(id+"F0.wireOp",EDGE,"E8.3.1"),sQuery(id+"F0.wireOp",EDGE,"E8.4.0"),sQuery(id+"F0.wireOp",EDGE,"E8.4.1"),sQuery(id+"F0.wireOp",EDGE,"E8.5.0"),sQuery(id+"F0.wireOp",EDGE,"E8.5.1"),sQuery(id+"F0.wireOp",EDGE,"E8.6.0"),sQuery(id+"F0.wireOp",EDGE,"E8.6.1"),sQuery(id+"F0.wireOp",EDGE,"E8.7.0"),sQuery(id+"F0.wireOp",EDGE,"E8.7.1"),sQuery(id+"F0.wireOp",EDGE,"E8.8.0"),sQuery(id+"F0.wireOp",EDGE,"E8.8.1"),sQuery(id+"F0.wireOp",EDGE,"E8.9.0"),sQuery(id+"F0.wireOp",EDGE,"E8.9.1"),sQuery(id+"F0.wireOp",EDGE,"E8.10.0"),sQuery(id+"F0.wireOp",EDGE,"E8.10.1"),sQuery(id+"F0.wireOp",EDGE,"E8.11.0"),sQuery(id+"F0.wireOp",EDGE,"E8.11.1"),sQuery(id+"F0.wireOp",EDGE,"E10")])]}),"instanceName":"1"});
            var Q1;
            Q1=makeQuery(id+"F1.opExtrude","SWEPT_BODY",BODY,{"disambiguationData":[OSD([sQuery(id+"F0.wireOp",EDGE,"E2"),sQuery(id+"F0.wireOp",EDGE,"E3"),sQuery(id+"F0.wireOp",EDGE,"E4"),sQuery(id+"F0.wireOp",EDGE,"E5"),sQuery(id+"F0.wireOp",EDGE,"E8.1.0"),sQuery(id+"F0.wireOp",EDGE,"E8.1.1"),sQuery(id+"F0.wireOp",EDGE,"E8.2.0"),sQuery(id+"F0.wireOp",EDGE,"E8.2.1"),sQuery(id+"F0.wireOp",EDGE,"E8.3.0"),sQuery(id+"F0.wireOp",EDGE,"E8.3.1"),sQuery(id+"F0.wireOp",EDGE,"E8.4.0"),sQuery(id+"F0.wireOp",EDGE,"E8.4.1"),sQuery(id+"F0.wireOp",EDGE,"E8.5.0"),sQuery(id+"F0.wireOp",EDGE,"E8.5.1"),sQuery(id+"F0.wireOp",EDGE,"E8.6.0"),sQuery(id+"F0.wireOp",EDGE,"E8.6.1"),sQuery(id+"F0.wireOp",EDGE,"E8.7.0"),sQuery(id+"F0.wireOp",EDGE,"E8.7.1"),sQuery(id+"F0.wireOp",EDGE,"E8.8.0"),sQuery(id+"F0.wireOp",EDGE,"E8.8.1"),sQuery(id+"F0.wireOp",EDGE,"E8.9.0"),sQuery(id+"F0.wireOp",EDGE,"E8.9.1"),sQuery(id+"F0.wireOp",EDGE,"E8.10.0"),sQuery(id+"F0.wireOp",EDGE,"E8.10.1"),sQuery(id+"F0.wireOp",EDGE,"E8.11.0"),sQuery(id+"F0.wireOp",EDGE,"E8.11.1"),sQuery(id+"F0.wireOp",EDGE,"E10")])]});
            var Q2;
            Q2=makeQuery(id+"F10.opPattern","COPY",BODY,{"derivedFrom":makeQuery(id+"F2.opExtrude","SWEPT_BODY",BODY,{"disambiguationData":[OSD([sQuery(id+"F0.wireOp",EDGE,"E0"),sQuery(id+"F0.wireOp",EDGE,"E1"),sQuery(id+"F0.wireOp",EDGE,"E6"),sQuery(id+"F0.wireOp",EDGE,"E7"),sQuery(id+"F0.wireOp",EDGE,"E9.1.0"),sQuery(id+"F0.wireOp",EDGE,"E9.1.1"),sQuery(id+"F0.wireOp",EDGE,"E9.2.0"),sQuery(id+"F0.wireOp",EDGE,"E9.2.1"),sQuery(id+"F0.wireOp",EDGE,"E9.3.0"),sQuery(id+"F0.wireOp",EDGE,"E9.3.1"),sQuery(id+"F0.wireOp",EDGE,"E9.4.0"),sQuery(id+"F0.wireOp",EDGE,"E9.4.1"),sQuery(id+"F0.wireOp",EDGE,"E9.5.0"),sQuery(id+"F0.wireOp",EDGE,"E9.5.1"),sQuery(id+"F0.wireOp",EDGE,"E9.6.0"),sQuery(id+"F0.wireOp",EDGE,"E9.6.1"),sQuery(id+"F0.wireOp",EDGE,"E9.7.0"),sQuery(id+"F0.wireOp",EDGE,"E9.7.1"),sQuery(id+"F0.wireOp",EDGE,"E9.8.0"),sQuery(id+"F0.wireOp",EDGE,"E9.8.1"),sQuery(id+"F0.wireOp",EDGE,"E9.9.0"),sQuery(id+"F0.wireOp",EDGE,"E9.9.1"),sQuery(id+"F0.wireOp",EDGE,"E9.10.0"),sQuery(id+"F0.wireOp",EDGE,"E9.10.1"),sQuery(id+"F0.wireOp",EDGE,"E9.11.0"),sQuery(id+"F0.wireOp",EDGE,"E9.11.1"),sQuery(id+"F0.wireOp",EDGE,"E9.12.0"),sQuery(id+"F0.wireOp",EDGE,"E9.12.1"),sQuery(id+"F0.wireOp",EDGE,"E9.13.0"),sQuery(id+"F0.wireOp",EDGE,"E9.13.1"),sQuery(id+"F0.wireOp",EDGE,"E9.14.0"),sQuery(id+"F0.wireOp",EDGE,"E9.14.1"),sQuery(id+"F0.wireOp",EDGE,"E9.15.0"),sQuery(id+"F0.wireOp",EDGE,"E9.15.1"),sQuery(id+"F0.wireOp",EDGE,"E9.16.0"),sQuery(id+"F0.wireOp",EDGE,"E9.16.1"),sQuery(id+"F0.wireOp",EDGE,"E9.17.0"),sQuery(id+"F0.wireOp",EDGE,"E9.17.1"),sQuery(id+"F0.wireOp",EDGE,"E11")])]}),"instanceName":"1"});
            var Q3;
            Q3=makeQuery(id+"F2.opExtrude","SWEPT_BODY",BODY,{"disambiguationData":[OSD([sQuery(id+"F0.wireOp",EDGE,"E0"),sQuery(id+"F0.wireOp",EDGE,"E1"),sQuery(id+"F0.wireOp",EDGE,"E6"),sQuery(id+"F0.wireOp",EDGE,"E7"),sQuery(id+"F0.wireOp",EDGE,"E9.1.0"),sQuery(id+"F0.wireOp",EDGE,"E9.1.1"),sQuery(id+"F0.wireOp",EDGE,"E9.2.0"),sQuery(id+"F0.wireOp",EDGE,"E9.2.1"),sQuery(id+"F0.wireOp",EDGE,"E9.3.0"),sQuery(id+"F0.wireOp",EDGE,"E9.3.1"),sQuery(id+"F0.wireOp",EDGE,"E9.4.0"),sQuery(id+"F0.wireOp",EDGE,"E9.4.1"),sQuery(id+"F0.wireOp",EDGE,"E9.5.0"),sQuery(id+"F0.wireOp",EDGE,"E9.5.1"),sQuery(id+"F0.wireOp",EDGE,"E9.6.0"),sQuery(id+"F0.wireOp",EDGE,"E9.6.1"),sQuery(id+"F0.wireOp",EDGE,"E9.7.0"),sQuery(id+"F0.wireOp",EDGE,"E9.7.1"),sQuery(id+"F0.wireOp",EDGE,"E9.8.0"),sQuery(id+"F0.wireOp",EDGE,"E9.8.1"),sQuery(id+"F0.wireOp",EDGE,"E9.9.0"),sQuery(id+"F0.wireOp",EDGE,"E9.9.1"),sQuery(id+"F0.wireOp",EDGE,"E9.10.0"),sQuery(id+"F0.wireOp",EDGE,"E9.10.1"),sQuery(id+"F0.wireOp",EDGE,"E9.11.0"),sQuery(id+"F0.wireOp",EDGE,"E9.11.1"),sQuery(id+"F0.wireOp",EDGE,"E9.12.0"),sQuery(id+"F0.wireOp",EDGE,"E9.12.1"),sQuery(id+"F0.wireOp",EDGE,"E9.13.0"),sQuery(id+"F0.wireOp",EDGE,"E9.13.1"),sQuery(id+"F0.wireOp",EDGE,"E9.14.0"),sQuery(id+"F0.wireOp",EDGE,"E9.14.1"),sQuery(id+"F0.wireOp",EDGE,"E9.15.0"),sQuery(id+"F0.wireOp",EDGE,"E9.15.1"),sQuery(id+"F0.wireOp",EDGE,"E9.16.0"),sQuery(id+"F0.wireOp",EDGE,"E9.16.1"),sQuery(id+"F0.wireOp",EDGE,"E9.17.0"),sQuery(id+"F0.wireOp",EDGE,"E9.17.1"),sQuery(id+"F0.wireOp",EDGE,"E11")])]});
            var Q4;
            Q4=sQuery(id+"F13.wireOp",EDGE,"E12");
            transform(context, id + "F14", {"entities" : qUnion([Q0, Q1, Q2, Q3]), "transformType" : TransformType.ROTATION, "transformAxis" : qUnion([Q4]), "angle" : 180 * degree, "makeCopy" : true});
        }
        {
            var Q0;
            Q0=makeQuery(id+"F14.opPattern","COPY",BODY,{"derivedFrom":makeQuery(id+"F1.opExtrude","SWEPT_BODY",BODY,{"disambiguationData":[OSD([sQuery(id+"F0.wireOp",EDGE,"E2"),sQuery(id+"F0.wireOp",EDGE,"E3"),sQuery(id+"F0.wireOp",EDGE,"E4"),sQuery(id+"F0.wireOp",EDGE,"E5"),sQuery(id+"F0.wireOp",EDGE,"E8.1.0"),sQuery(id+"F0.wireOp",EDGE,"E8.1.1"),sQuery(id+"F0.wireOp",EDGE,"E8.2.0"),sQuery(id+"F0.wireOp",EDGE,"E8.2.1"),sQuery(id+"F0.wireOp",EDGE,"E8.3.0"),sQuery(id+"F0.wireOp",EDGE,"E8.3.1"),sQuery(id+"F0.wireOp",EDGE,"E8.4.0"),sQuery(id+"F0.wireOp",EDGE,"E8.4.1"),sQuery(id+"F0.wireOp",EDGE,"E8.5.0"),sQuery(id+"F0.wireOp",EDGE,"E8.5.1"),sQuery(id+"F0.wireOp",EDGE,"E8.6.0"),sQuery(id+"F0.wireOp",EDGE,"E8.6.1"),sQuery(id+"F0.wireOp",EDGE,"E8.7.0"),sQuery(id+"F0.wireOp",EDGE,"E8.7.1"),sQuery(id+"F0.wireOp",EDGE,"E8.8.0"),sQuery(id+"F0.wireOp",EDGE,"E8.8.1"),sQuery(id+"F0.wireOp",EDGE,"E8.9.0"),sQuery(id+"F0.wireOp",EDGE,"E8.9.1"),sQuery(id+"F0.wireOp",EDGE,"E8.10.0"),sQuery(id+"F0.wireOp",EDGE,"E8.10.1"),sQuery(id+"F0.wireOp",EDGE,"E8.11.0"),sQuery(id+"F0.wireOp",EDGE,"E8.11.1"),sQuery(id+"F0.wireOp",EDGE,"E10")])]}),"instanceName":"1"});
            var Q1;
            Q1=makeQuery(id+"F14.opPattern","COPY",BODY,{"derivedFrom":makeQuery(id+"F10.opPattern","COPY",BODY,{"derivedFrom":makeQuery(id+"F1.opExtrude","SWEPT_BODY",BODY,{"disambiguationData":[OSD([sQuery(id+"F0.wireOp",EDGE,"E2"),sQuery(id+"F0.wireOp",EDGE,"E3"),sQuery(id+"F0.wireOp",EDGE,"E4"),sQuery(id+"F0.wireOp",EDGE,"E5"),sQuery(id+"F0.wireOp",EDGE,"E8.1.0"),sQuery(id+"F0.wireOp",EDGE,"E8.1.1"),sQuery(id+"F0.wireOp",EDGE,"E8.2.0"),sQuery(id+"F0.wireOp",EDGE,"E8.2.1"),sQuery(id+"F0.wireOp",EDGE,"E8.3.0"),sQuery(id+"F0.wireOp",EDGE,"E8.3.1"),sQuery(id+"F0.wireOp",EDGE,"E8.4.0"),sQuery(id+"F0.wireOp",EDGE,"E8.4.1"),sQuery(id+"F0.wireOp",EDGE,"E8.5.0"),sQuery(id+"F0.wireOp",EDGE,"E8.5.1"),sQuery(id+"F0.wireOp",EDGE,"E8.6.0"),sQuery(id+"F0.wireOp",EDGE,"E8.6.1"),sQuery(id+"F0.wireOp",EDGE,"E8.7.0"),sQuery(id+"F0.wireOp",EDGE,"E8.7.1"),sQuery(id+"F0.wireOp",EDGE,"E8.8.0"),sQuery(id+"F0.wireOp",EDGE,"E8.8.1"),sQuery(id+"F0.wireOp",EDGE,"E8.9.0"),sQuery(id+"F0.wireOp",EDGE,"E8.9.1"),sQuery(id+"F0.wireOp",EDGE,"E8.10.0"),sQuery(id+"F0.wireOp",EDGE,"E8.10.1"),sQuery(id+"F0.wireOp",EDGE,"E8.11.0"),sQuery(id+"F0.wireOp",EDGE,"E8.11.1"),sQuery(id+"F0.wireOp",EDGE,"E10")])]}),"instanceName":"1"}),"instanceName":"1"});
            var Q2;
            Q2=makeQuery(id+"F14.opPattern","COPY",EDGE,{"derivedFrom":makeQuery(id+"F10.opPattern","COPY",EDGE,{"derivedFrom":makeQuery(id+"F1.opExtrude","CAP_EDGE",EDGE,{"disambiguationData":[OSD([sQuery(id+"F0.wireOp",EDGE,"E3")])],"isStart":false}),"instanceName":"1"}),"instanceName":"1"});
            transform(context, id + "F15", {"entities" : qUnion([Q0, Q1]), "transformType" : TransformType.ROTATION, "transformAxis" : qUnion([Q2]), "angle" : 7.5 * degree, "makeCopy" : false});
        }
        {
            var Q0;
            Q0=makeQuery(id+"F14.opPattern","COPY",BODY,{"derivedFrom":makeQuery(id+"F2.opExtrude","SWEPT_BODY",BODY,{"disambiguationData":[OSD([sQuery(id+"F0.wireOp",EDGE,"E0"),sQuery(id+"F0.wireOp",EDGE,"E1"),sQuery(id+"F0.wireOp",EDGE,"E6"),sQuery(id+"F0.wireOp",EDGE,"E7"),sQuery(id+"F0.wireOp",EDGE,"E9.1.0"),sQuery(id+"F0.wireOp",EDGE,"E9.1.1"),sQuery(id+"F0.wireOp",EDGE,"E9.2.0"),sQuery(id+"F0.wireOp",EDGE,"E9.2.1"),sQuery(id+"F0.wireOp",EDGE,"E9.3.0"),sQuery(id+"F0.wireOp",EDGE,"E9.3.1"),sQuery(id+"F0.wireOp",EDGE,"E9.4.0"),sQuery(id+"F0.wireOp",EDGE,"E9.4.1"),sQuery(id+"F0.wireOp",EDGE,"E9.5.0"),sQuery(id+"F0.wireOp",EDGE,"E9.5.1"),sQuery(id+"F0.wireOp",EDGE,"E9.6.0"),sQuery(id+"F0.wireOp",EDGE,"E9.6.1"),sQuery(id+"F0.wireOp",EDGE,"E9.7.0"),sQuery(id+"F0.wireOp",EDGE,"E9.7.1"),sQuery(id+"F0.wireOp",EDGE,"E9.8.0"),sQuery(id+"F0.wireOp",EDGE,"E9.8.1"),sQuery(id+"F0.wireOp",EDGE,"E9.9.0"),sQuery(id+"F0.wireOp",EDGE,"E9.9.1"),sQuery(id+"F0.wireOp",EDGE,"E9.10.0"),sQuery(id+"F0.wireOp",EDGE,"E9.10.1"),sQuery(id+"F0.wireOp",EDGE,"E9.11.0"),sQuery(id+"F0.wireOp",EDGE,"E9.11.1"),sQuery(id+"F0.wireOp",EDGE,"E9.12.0"),sQuery(id+"F0.wireOp",EDGE,"E9.12.1"),sQuery(id+"F0.wireOp",EDGE,"E9.13.0"),sQuery(id+"F0.wireOp",EDGE,"E9.13.1"),sQuery(id+"F0.wireOp",EDGE,"E9.14.0"),sQuery(id+"F0.wireOp",EDGE,"E9.14.1"),sQuery(id+"F0.wireOp",EDGE,"E9.15.0"),sQuery(id+"F0.wireOp",EDGE,"E9.15.1"),sQuery(id+"F0.wireOp",EDGE,"E9.16.0"),sQuery(id+"F0.wireOp",EDGE,"E9.16.1"),sQuery(id+"F0.wireOp",EDGE,"E9.17.0"),sQuery(id+"F0.wireOp",EDGE,"E9.17.1"),sQuery(id+"F0.wireOp",EDGE,"E11")])]}),"instanceName":"1"});
            var Q1;
            Q1=makeQuery(id+"F14.opPattern","COPY",BODY,{"derivedFrom":makeQuery(id+"F10.opPattern","COPY",BODY,{"derivedFrom":makeQuery(id+"F2.opExtrude","SWEPT_BODY",BODY,{"disambiguationData":[OSD([sQuery(id+"F0.wireOp",EDGE,"E0"),sQuery(id+"F0.wireOp",EDGE,"E1"),sQuery(id+"F0.wireOp",EDGE,"E6"),sQuery(id+"F0.wireOp",EDGE,"E7"),sQuery(id+"F0.wireOp",EDGE,"E9.1.0"),sQuery(id+"F0.wireOp",EDGE,"E9.1.1"),sQuery(id+"F0.wireOp",EDGE,"E9.2.0"),sQuery(id+"F0.wireOp",EDGE,"E9.2.1"),sQuery(id+"F0.wireOp",EDGE,"E9.3.0"),sQuery(id+"F0.wireOp",EDGE,"E9.3.1"),sQuery(id+"F0.wireOp",EDGE,"E9.4.0"),sQuery(id+"F0.wireOp",EDGE,"E9.4.1"),sQuery(id+"F0.wireOp",EDGE,"E9.5.0"),sQuery(id+"F0.wireOp",EDGE,"E9.5.1"),sQuery(id+"F0.wireOp",EDGE,"E9.6.0"),sQuery(id+"F0.wireOp",EDGE,"E9.6.1"),sQuery(id+"F0.wireOp",EDGE,"E9.7.0"),sQuery(id+"F0.wireOp",EDGE,"E9.7.1"),sQuery(id+"F0.wireOp",EDGE,"E9.8.0"),sQuery(id+"F0.wireOp",EDGE,"E9.8.1"),sQuery(id+"F0.wireOp",EDGE,"E9.9.0"),sQuery(id+"F0.wireOp",EDGE,"E9.9.1"),sQuery(id+"F0.wireOp",EDGE,"E9.10.0"),sQuery(id+"F0.wireOp",EDGE,"E9.10.1"),sQuery(id+"F0.wireOp",EDGE,"E9.11.0"),sQuery(id+"F0.wireOp",EDGE,"E9.11.1"),sQuery(id+"F0.wireOp",EDGE,"E9.12.0"),sQuery(id+"F0.wireOp",EDGE,"E9.12.1"),sQuery(id+"F0.wireOp",EDGE,"E9.13.0"),sQuery(id+"F0.wireOp",EDGE,"E9.13.1"),sQuery(id+"F0.wireOp",EDGE,"E9.14.0"),sQuery(id+"F0.wireOp",EDGE,"E9.14.1"),sQuery(id+"F0.wireOp",EDGE,"E9.15.0"),sQuery(id+"F0.wireOp",EDGE,"E9.15.1"),sQuery(id+"F0.wireOp",EDGE,"E9.16.0"),sQuery(id+"F0.wireOp",EDGE,"E9.16.1"),sQuery(id+"F0.wireOp",EDGE,"E9.17.0"),sQuery(id+"F0.wireOp",EDGE,"E9.17.1"),sQuery(id+"F0.wireOp",EDGE,"E11")])]}),"instanceName":"1"}),"instanceName":"1"});
            var Q2;
            Q2=makeQuery(id+"F14.opPattern","COPY",EDGE,{"derivedFrom":makeQuery(id+"F10.opPattern","COPY",EDGE,{"derivedFrom":makeQuery(id+"F2.opExtrude","CAP_EDGE",EDGE,{"disambiguationData":[OSD([sQuery(id+"F0.wireOp",EDGE,"E0")])],"isStart":false}),"instanceName":"1"}),"instanceName":"1"});
            transform(context, id + "F16", {"entities" : qUnion([Q0, Q1]), "transformType" : TransformType.ROTATION, "transformAxis" : qUnion([Q2]), "angle" : 5 * degree, "makeCopy" : false});
        }
    });
